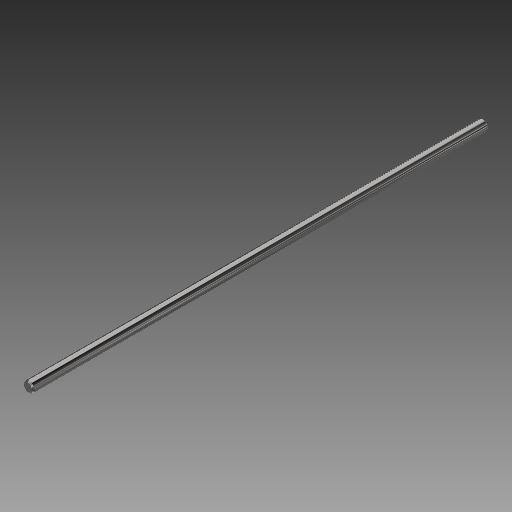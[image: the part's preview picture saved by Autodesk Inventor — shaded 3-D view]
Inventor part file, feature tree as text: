
AUTODESK INVENTOR PART (.ipt)
format: ipt  version: 2019 (Build 230136000, 136)  size: 86,016 bytes
history: native  units: mm
features: extrude x1, chamfer x1, sketch x1
ambient origin geometry x8: Origin, YZ Plane, XZ Plane, XY Plane, X Axis, Y Axis, Z Axis, Center Point
bodies: Solid1 (feature_tree)
feature tree (3):
  extrude  "Extrusion1"  Depth=345.0mm TaperAngle=0.0deg
  chamfer  "Chamfer1"  Distance=1.0mm Angle=45.0deg
  sketch  "Sketch1"  dims[d0=8.0mm d1=345.0mm d2=0.0mm d3=1.0mm d4=2.0mm d5=45.0deg]
